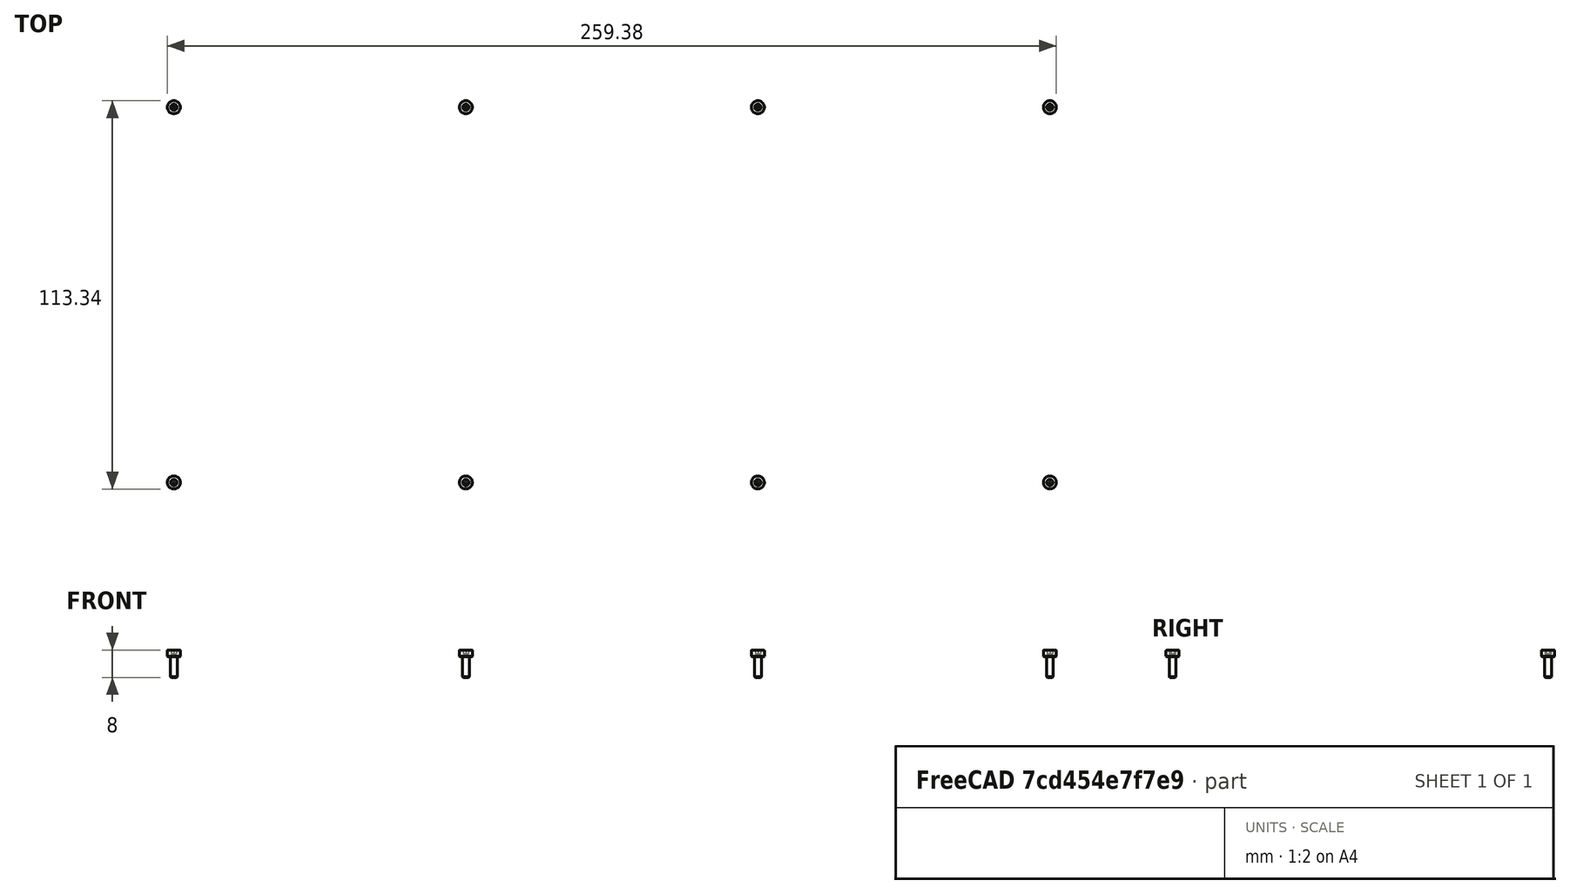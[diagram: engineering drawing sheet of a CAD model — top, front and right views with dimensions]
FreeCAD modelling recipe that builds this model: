
FCSTD DOCUMENT  (FreeCAD 0.19R23141 (Git))
Label: L32_Squash
License: Creative Commons Attribution-NonCommercial 4.0 International License.
LicenseURL: http://creativecommons.org/licenses/by-nc/4.0/
objects: App::Link×13, TechDraw::DrawViewPart×9, Part::FeaturePython×8, App::DocumentObjectGroup×2, PartDesign::CoordinateSystem×1, App::FeaturePython×1, App::Part×1, TechDraw::DrawSVGTemplate×1, TechDraw::DrawPage×1
note: 9 computed B-rep shape members (.brp) not serialized (recipe doc carries the construction recipe, not evaluated geometry)
EXTERNAL_REF file=O56_BottomPlate.FCStd obj=LCS_0
EXTERNAL_REF file=O56_BottomPlate.FCStd obj=Part
EXTERNAL_REF file=Y7X_ClosedSpacer.FCStd obj=LCS_0
EXTERNAL_REF file=Y7X_ClosedSpacer.FCStd obj=Part
EXTERNAL_REF file=D65_USBCutoutSpacer.FCStd obj=LCS_0
EXTERNAL_REF file=D65_USBCutoutSpacer.FCStd obj=Part
EXTERNAL_REF file=S86_SwitchPlate.FCStd obj=LCS_0
EXTERNAL_REF file=S86_SwitchPlate.FCStd obj=Part
EXTERNAL_REF file=Q45_OLEDCover.FCStd obj=LCS_0
EXTERNAL_REF file=Q45_OLEDCover.FCStd obj=Part
EXTERNAL_REF file=O03_TopCover.FCStd obj=LCS_0
EXTERNAL_REF file=O03_TopCover.FCStd obj=Part
EXTERNAL_REF file=O03_TopCover.FCStd obj=LCS_1
EXTERNAL_REF file=O03_TopCover.FCStd obj=LCS_2
EXTERNAL_REF file=O03_TopCover.FCStd obj=LCS_3
EXTERNAL_REF file=O03_TopCover.FCStd obj=LCS_4
EXTERNAL_REF file=O03_TopCover.FCStd obj=LCS_5
EXTERNAL_REF file=O03_TopCover.FCStd obj=LCS_6
EXTERNAL_REF file=O03_TopCover.FCStd obj=LCS_7
EXTERNAL_REF file=O03_TopCover.FCStd obj=LCS_8
EXTERNAL_REF file=R79_SquashPCB.FCStd obj=LCS_0
EXTERNAL_REF file=R79_SquashPCB.FCStd obj=Part
EXTERNAL_REF file=D19_Ssd1306Oled128x32.FCStd obj=LCS_1
EXTERNAL_REF file=R79_SquashPCB.FCStd obj=OLEDPin
EXTERNAL_REF file=D19_Ssd1306Oled128x32.FCStd obj=Part
EXTERNAL_REF file=X21_Foot0.FCStd obj=LCS_0
EXTERNAL_REF file=X21_Foot0.FCStd obj=Part
EXTERNAL_REF file=X22_Foot1.FCStd obj=LCS_0
EXTERNAL_REF file=X22_Foot1.FCStd obj=Part
EXTERNAL_REF file=X23_Foot2.FCStd obj=LCS_0
EXTERNAL_REF file=X23_Foot2.FCStd obj=Part

FEATURE [App::DocumentObjectGroup] Parts
FEATURE [PartDesign::CoordinateSystem] LCS_Origin
  AttacherType = Attacher::AttachEngine3D
  MapMode = 2
  Support = -> [X_Axis]
FEATURE [App::DocumentObjectGroup] Constraints
FEATURE [App::FeaturePython] Variables  # WARN: FeaturePython — macro-defined, semantics opaque (R4)
FEATURE [App::Link] O56_BottomPlate_Part
  AssemblyType = Asm4EE
  AttachedBy = #LCS_0
  AttachedTo = Parent Assembly#LCS_Origin
  ElementCount = 0
  LinkTransform = false
  Scale = 1
  ScaleVector = (1,1,1)
  ShowElement = true
  expr: Placement = LCS_Origin.Placement * AttachmentOffset * O56_BottomPlate#LCS_0.Placement ^ -1
FEATURE [App::Link] Y7X_ClosedSpacer_Part
  AssemblyType = Asm4EE
  AttachedBy = #LCS_0
  AttachedTo = Parent Assembly#LCS_Origin
  AttachmentOffset = pos=(0,0,3.175) rot=(0,0,1;0rad)
  ElementCount = 0
  LinkPlacement = pos=(0,0,3.175) rot=(0,0,1;0rad)
  LinkTransform = false
  Placement = pos=(0,0,3.175) rot=(0,0,1;0rad)
  Scale = 1
  ScaleVector = (1,1,1)
  ShowElement = true
  expr: Placement = LCS_Origin.Placement * AttachmentOffset * Y7X_ClosedSpacer#LCS_0.Placement ^ -1
FEATURE [App::Link] D65_USBCutoutSpacer_Part
  AssemblyType = Asm4EE
  AttachedBy = #LCS_0
  AttachedTo = Parent Assembly#LCS_Origin
  AttachmentOffset = pos=(0,0,6.35) rot=(0,0,1;0rad)
  ElementCount = 0
  LinkPlacement = pos=(0,0,6.35) rot=(0,0,1;0rad)
  LinkTransform = false
  Placement = pos=(0,0,6.35) rot=(0,0,1;0rad)
  Scale = 1
  ScaleVector = (1,1,1)
  ShowElement = true
  expr: Placement = LCS_Origin.Placement * AttachmentOffset * D65_USBCutoutSpacer#LCS_0.Placement ^ -1
FEATURE [App::Link] D65_USBCutoutSpacer_Part001
  AssemblyType = Asm4EE
  AttachedBy = #LCS_0
  AttachedTo = Parent Assembly#LCS_Origin
  AttachmentOffset = pos=(0,0,9.525) rot=(0,0,1;0rad)
  ElementCount = 0
  LinkPlacement = pos=(0,0,9.525) rot=(0,0,1;0rad)
  LinkTransform = false
  Placement = pos=(0,0,9.525) rot=(0,0,1;0rad)
  Scale = 1
  ScaleVector = (1,1,1)
  ShowElement = true
  expr: Placement = LCS_Origin.Placement * AttachmentOffset * D65_USBCutoutSpacer#LCS_0.Placement ^ -1
FEATURE [App::Link] S86_SwitchPlate_Part
  AssemblyType = Asm4EE
  AttachedBy = #LCS_0
  AttachedTo = Parent Assembly#LCS_Origin
  AttachmentOffset = pos=(0,0,12.7) rot=(0,0,1;0rad)
  ElementCount = 0
  LinkPlacement = pos=(0,0,12.7) rot=(0,0,1;0rad)
  LinkTransform = false
  Placement = pos=(0,0,12.7) rot=(0,0,1;0rad)
  Scale = 1
  ScaleVector = (1,1,1)
  ShowElement = true
  expr: Placement = LCS_Origin.Placement * AttachmentOffset * S86_SwitchPlate#LCS_0.Placement ^ -1
FEATURE [App::Link] Y7X_ClosedSpacer_Part001
  AssemblyType = Asm4EE
  AttachedBy = #LCS_0
  AttachedTo = Parent Assembly#LCS_Origin
  AttachmentOffset = pos=(0,0,14.2875) rot=(0,0,1;0rad)
  ElementCount = 0
  LinkPlacement = pos=(0,0,14.2875) rot=(0,0,1;0rad)
  LinkTransform = false
  Placement = pos=(0,0,14.2875) rot=(0,0,1;0rad)
  Scale = 1
  ScaleVector = (1,1,1)
  ShowElement = true
  expr: Placement = LCS_Origin.Placement * AttachmentOffset * Y7X_ClosedSpacer#LCS_0.Placement ^ -1
FEATURE [App::Link] Q45_OLEDCover_Part
  AssemblyType = Asm4EE
  AttachedBy = #LCS_0
  AttachedTo = Parent Assembly#LCS_Origin
  AttachmentOffset = pos=(0,0,17.4625) rot=(0,0,1;0rad)
  ElementCount = 0
  LinkPlacement = pos=(0,0,17.4625) rot=(0,0,1;0rad)
  LinkTransform = false
  Placement = pos=(0,0,17.4625) rot=(0,0,1;0rad)
  Scale = 1
  ScaleVector = (1,1,1)
  ShowElement = true
  expr: .AttachmentOffset.Base.z = 0.125in * 5 + 0.0625in * 1
  expr: Placement = LCS_Origin.Placement * AttachmentOffset * Q45_OLEDCover#LCS_0.Placement ^ -1
FEATURE [App::Link] O03_TopCover_Part
  AssemblyType = Asm4EE
  AttachedBy = #LCS_0
  AttachedTo = Parent Assembly#LCS_Origin
  AttachmentOffset = pos=(0,0,20.6375) rot=(0,0,1;0rad)
  ElementCount = 0
  LinkPlacement = pos=(0,0,20.6375) rot=(0,0,1;0rad)
  LinkTransform = false
  Placement = pos=(0,0,20.6375) rot=(0,0,1;0rad)
  Scale = 1
  ScaleVector = (1,1,1)
  ShowElement = true
  expr: .AttachmentOffset.Base.z = 0.125in * 6 + 0.0625in * 1
  expr: Placement = LCS_Origin.Placement * AttachmentOffset * O03_TopCover#LCS_0.Placement ^ -1
FEATURE [Part::FeaturePython] Screw  label="M2x6-Screw001"  # WARN: FeaturePython — macro-defined, semantics opaque (R4)
  AssemblyType = Asm4EE
  AttachedBy = Origin
  AttachedTo = O03_TopCover_Part#LCS_1
  Placement = pos=(-127.794,54.7687,23.8125) rot=(0,0,1;1.5708rad)
  diameter = 2
  invert = false
  length = 3
  lengthCustom = 6
  matchOuter = false
  offset = 0
  thread = false
  type = 32
  expr: Placement = O03_TopCover_Part.Placement * O03_TopCover#LCS_1.Placement * AttachmentOffset
FEATURE [Part::FeaturePython] Screw003  label="M2x6-Screw"  # WARN: FeaturePython — macro-defined, semantics opaque (R4)
  AssemblyType = Asm4EE
  AttachedBy = Origin
  AttachedTo = O03_TopCover_Part#LCS_2
  Placement = pos=(-42.5979,54.7687,23.8125) rot=(0,0,1;1.5708rad)
  diameter = 2
  invert = false
  length = 3
  lengthCustom = 6
  matchOuter = false
  offset = 0
  thread = false
  type = 32
  expr: Placement = O03_TopCover_Part.Placement * O03_TopCover#LCS_2.Placement * AttachmentOffset
FEATURE [Part::FeaturePython] Screw004  label="M2x6-Screw002"  # WARN: FeaturePython — macro-defined, semantics opaque (R4)
  AssemblyType = Asm4EE
  AttachedBy = Origin
  AttachedTo = O03_TopCover_Part#LCS_3
  Placement = pos=(42.5979,54.7687,23.8125) rot=(0,0,1;1.5708rad)
  diameter = 2
  invert = false
  length = 3
  lengthCustom = 6
  matchOuter = false
  offset = 0
  thread = false
  type = 32
  expr: Placement = O03_TopCover_Part.Placement * O03_TopCover#LCS_3.Placement * AttachmentOffset
FEATURE [Part::FeaturePython] Screw005  label="M2x6-Screw003"  # WARN: FeaturePython — macro-defined, semantics opaque (R4)
  AssemblyType = Asm4EE
  AttachedBy = Origin
  AttachedTo = O03_TopCover_Part#LCS_4
  Placement = pos=(127.794,54.7687,23.8125) rot=(0,0,1;1.5708rad)
  diameter = 2
  invert = false
  length = 3
  lengthCustom = 6
  matchOuter = false
  offset = 0
  thread = false
  type = 32
  expr: Placement = O03_TopCover_Part.Placement * O03_TopCover#LCS_4.Placement * AttachmentOffset
FEATURE [Part::FeaturePython] Screw007  label="M2x6-Screw005"  # WARN: FeaturePython — macro-defined, semantics opaque (R4)
  AssemblyType = Asm4EE
  AttachedBy = Origin
  AttachedTo = O03_TopCover_Part#LCS_5
  Placement = pos=(127.794,-54.7687,23.8125) rot=(0,0,1;1.5708rad)
  diameter = 2
  invert = false
  length = 3
  lengthCustom = 6
  matchOuter = false
  offset = 0
  thread = false
  type = 32
  expr: Placement = O03_TopCover_Part.Placement * O03_TopCover#LCS_5.Placement * AttachmentOffset
FEATURE [Part::FeaturePython] Screw008  label="M2x6-Screw006"  # WARN: FeaturePython — macro-defined, semantics opaque (R4)
  AssemblyType = Asm4EE
  AttachedBy = Origin
  AttachedTo = O03_TopCover_Part#LCS_6
  Placement = pos=(42.5979,-54.7687,23.8125) rot=(0,0,1;1.5708rad)
  diameter = 2
  invert = false
  length = 3
  lengthCustom = 6
  matchOuter = false
  offset = 0
  thread = false
  type = 32
  expr: Placement = O03_TopCover_Part.Placement * O03_TopCover#LCS_6.Placement * AttachmentOffset
FEATURE [Part::FeaturePython] Screw009  label="M2x6-Screw007"  # WARN: FeaturePython — macro-defined, semantics opaque (R4)
  AssemblyType = Asm4EE
  AttachedBy = Origin
  AttachedTo = O03_TopCover_Part#LCS_7
  Placement = pos=(-42.5979,-54.7687,23.8125) rot=(0,0,1;1.5708rad)
  diameter = 2
  invert = false
  length = 3
  lengthCustom = 6
  matchOuter = false
  offset = 0
  thread = false
  type = 32
  expr: Placement = O03_TopCover_Part.Placement * O03_TopCover#LCS_7.Placement * AttachmentOffset
FEATURE [Part::FeaturePython] Screw010  label="M2x6-Screw008"  # WARN: FeaturePython — macro-defined, semantics opaque (R4)
  AssemblyType = Asm4EE
  AttachedBy = Origin
  AttachedTo = O03_TopCover_Part#LCS_8
  Placement = pos=(-127.794,-54.7687,23.8125) rot=(0,0,1;1.5708rad)
  diameter = 2
  invert = false
  length = 3
  lengthCustom = 6
  matchOuter = false
  offset = 0
  thread = false
  type = 32
  expr: Placement = O03_TopCover_Part.Placement * O03_TopCover#LCS_8.Placement * AttachmentOffset
FEATURE [App::Link] R79_SquashPCB_Part
  AssemblyType = Asm4EE
  AttachedBy = #LCS_0
  AttachedTo = S86_SwitchPlate_Part#LCS_0
  AttachmentOffset = pos=(0,0,-3.199) rot=(0,0,1;0rad)
  ElementCount = 0
  LinkPlacement = pos=(0,0,9.501) rot=(0,0,1;0rad)
  LinkTransform = false
  Placement = pos=(0,0,9.501) rot=(0,0,1;0rad)
  Scale = 1
  ScaleVector = (1,1,1)
  ShowElement = true
  expr: Placement = S86_SwitchPlate_Part.Placement * S86_SwitchPlate#LCS_0.Placement * AttachmentOffset * R79_SquashPCB#LCS_0.Placement ^ -1
FEATURE [App::Link] D19_Ssd1306Oled128x32_Part
  AssemblyType = Asm4EE
  AttachedBy = #LCS_1
  AttachedTo = R79_SquashPCB_Part#OLEDPin
  AttachmentOffset = pos=(0,0,4.25) rot=(0,0,1;0rad)
  ElementCount = 0
  LinkPlacement = pos=(-115.597,44.7858,13.751) rot=(0,0,1;0rad)
  LinkTransform = false
  Placement = pos=(-115.597,44.7858,13.751) rot=(0,0,1;0rad)
  Scale = 1
  ScaleVector = (1,1,1)
  ShowElement = true
  expr: Placement = R79_SquashPCB_Part.Placement * R79_SquashPCB#OLEDPin.Placement * AttachmentOffset * D19_Ssd1306Oled128x32#LCS_1.Placement ^ -1
FEATURE [App::Link] X21_Foot0_Part
  AssemblyType = Asm4EE
  AttachedBy = #LCS_0
  AttachedTo = Parent Assembly#LCS_Origin
  AttachmentOffset = pos=(0,31.75,-3.175) rot=(0,0,1;0rad)
  ElementCount = 0
  LinkPlacement = pos=(0,31.75,-3.175) rot=(0,0,1;0rad)
  LinkTransform = false
  Placement = pos=(0,31.75,-3.175) rot=(0,0,1;0rad)
  Scale = 1
  ScaleVector = (1,1,1)
  ShowElement = true
  expr: Placement = LCS_Origin.Placement * AttachmentOffset * X21_Foot0#LCS_0.Placement ^ -1
FEATURE [App::Link] X22_Foot1_Part
  AssemblyType = Asm4EE
  AttachedBy = #LCS_0
  AttachedTo = Parent Assembly#LCS_Origin
  AttachmentOffset = pos=(0,31.75,-6.35) rot=(0,0,1;0rad)
  ElementCount = 0
  LinkPlacement = pos=(0,31.75,-6.35) rot=(0,0,1;0rad)
  LinkTransform = false
  Placement = pos=(0,31.75,-6.35) rot=(0,0,1;0rad)
  Scale = 1
  ScaleVector = (1,1,1)
  ShowElement = true
  expr: Placement = LCS_Origin.Placement * AttachmentOffset * X22_Foot1#LCS_0.Placement ^ -1
FEATURE [App::Link] X23_Foot2_Part
  AssemblyType = Asm4EE
  AttachedBy = #LCS_0
  AttachedTo = Parent Assembly#LCS_Origin
  AttachmentOffset = pos=(0,31.75,-9.525) rot=(0,0,1;0rad)
  ElementCount = 0
  LinkPlacement = pos=(0,31.75,-9.525) rot=(0,0,1;0rad)
  LinkTransform = false
  Placement = pos=(0,31.75,-9.525) rot=(0,0,1;0rad)
  Scale = 1
  ScaleVector = (1,1,1)
  ShowElement = true
  expr: Placement = LCS_Origin.Placement * AttachmentOffset * X23_Foot2#LCS_0.Placement ^ -1
FEATURE [App::Part] Model
  Configuration = 0
  Group = -> [LCS_Origin,Constraints,Variables,O56_BottomPlate_Part,Y7X_ClosedSpacer_Part,D65_USBCutoutSpacer_Part,D65_USBCutoutSpacer_Part001,S86_SwitchPlate_Part,Y7X_ClosedSpacer_Part001,Q45_OLEDCover_Part,O03_TopCover_Part,Screw,Screw003,Screw004,Screw005,Screw007,Screw008,Screw009,Screw010,R79_SquashPCB_Part,D19_Ssd1306Oled128x32_Part,X21_Foot0_Part,X22_Foot1_Part,X23_Foot2_Part]
  Origin = -> Origin
  Type = Assembly4 Model
FEATURE [TechDraw::DrawSVGTemplate] Template
  Height = 841
  Orientation = 1
  Width = 1189
FEATURE [TechDraw::DrawViewPart] View
  CoarseView = false
  Direction = (0,0,1)
  Focus = 100
  HardHidden = false
  IsoCount = 0
  IsoHidden = false
  IsoVisible = false
  LockPosition = false
  Perspective = false
  Rotation = 0
  Scale = 1
  ScaleType = 0
  SeamHidden = false
  SeamVisible = true
  SmoothHidden = false
  SmoothVisible = true
  X = 147.151
  XDirection = (1,0,0)
  Y = 769.14
FEATURE [TechDraw::DrawViewPart] View001
  CoarseView = false
  Direction = (0,0,1)
  Focus = 100
  HardHidden = false
  IsoCount = 0
  IsoHidden = false
  IsoVisible = false
  LockPosition = false
  Perspective = false
  Rotation = 0
  Scale = 1
  ScaleType = 0
  SeamHidden = false
  SeamVisible = true
  SmoothHidden = false
  SmoothVisible = true
  X = 147.349
  XDirection = (1,0,0)
  Y = 629.763
FEATURE [TechDraw::DrawViewPart] View002
  CoarseView = false
  Direction = (0,0,1)
  Focus = 100
  HardHidden = false
  IsoCount = 0
  IsoHidden = false
  IsoVisible = false
  LockPosition = false
  Perspective = false
  Rotation = 0
  Scale = 1
  ScaleType = 0
  SeamHidden = false
  SeamVisible = true
  SmoothHidden = false
  SmoothVisible = true
  X = 147.349
  XDirection = (1,0,0)
  Y = 491.176
FEATURE [TechDraw::DrawViewPart] View003
  CoarseView = false
  Direction = (0,0,1)
  Focus = 100
  HardHidden = false
  IsoCount = 0
  IsoHidden = false
  IsoVisible = false
  LockPosition = false
  Perspective = false
  Rotation = 0
  Scale = 1
  ScaleType = 0
  SeamHidden = false
  SeamVisible = true
  SmoothHidden = false
  SmoothVisible = true
  X = 145.769
  XDirection = (1,0,0)
  Y = 89.0354
FEATURE [TechDraw::DrawViewPart] View004
  CoarseView = false
  Direction = (0,0,1)
  Focus = 100
  HardHidden = false
  IsoCount = 0
  IsoHidden = false
  IsoVisible = false
  LockPosition = false
  Perspective = false
  Rotation = 0
  Scale = 1
  ScaleType = 0
  SeamHidden = false
  SeamVisible = true
  SmoothHidden = false
  SmoothVisible = true
  X = 145.572
  XDirection = (1,0,0)
  Y = 355.352
FEATURE [TechDraw::DrawViewPart] View005
  CoarseView = false
  Direction = (0,0,1)
  Focus = 100
  HardHidden = false
  IsoCount = 0
  IsoHidden = false
  IsoVisible = false
  LockPosition = false
  Perspective = false
  Rotation = 0
  Scale = 1
  ScaleType = 0
  SeamHidden = false
  SeamVisible = true
  SmoothHidden = false
  SmoothVisible = true
  X = 144.387
  XDirection = (1,0,0)
  Y = 221.503
FEATURE [TechDraw::DrawViewPart] View006
  CoarseView = false
  Direction = (0,0,1)
  Focus = 100
  HardHidden = false
  IsoCount = 0
  IsoHidden = false
  IsoVisible = false
  LockPosition = false
  Perspective = false
  Rotation = 0
  Scale = 1
  ScaleType = 0
  SeamHidden = false
  SeamVisible = true
  SmoothHidden = false
  SmoothVisible = true
  X = 147.176
  XDirection = (1,0,0)
  Y = 522.376
FEATURE [TechDraw::DrawViewPart] View007
  CoarseView = false
  Direction = (0,0,1)
  Focus = 100
  HardHidden = false
  IsoCount = 0
  IsoHidden = false
  IsoVisible = false
  LockPosition = false
  Perspective = false
  Rotation = 0
  Scale = 1
  ScaleType = 0
  SeamHidden = false
  SeamVisible = true
  SmoothHidden = false
  SmoothVisible = true
  X = 148.531
  XDirection = (1,0,0)
  Y = 484.702
FEATURE [TechDraw::DrawViewPart] View008
  CoarseView = false
  Direction = (0,0,1)
  Focus = 100
  HardHidden = false
  IsoCount = 0
  IsoHidden = false
  IsoVisible = false
  LockPosition = false
  Perspective = false
  Rotation = 0
  Scale = 1
  ScaleType = 0
  SeamHidden = false
  SeamVisible = true
  SmoothHidden = false
  SmoothVisible = true
  X = 147.139
  XDirection = (1,0,0)
  Y = 454.245
FEATURE [TechDraw::DrawPage] Page
  KeepUpdated = true
  NextBalloonIndex = 1
  ProjectionType = 0
  Scale = 1
  Template = -> Template
  Views = -> [View,View001,View002,View003,View004,View005,View006,View007,View008]
